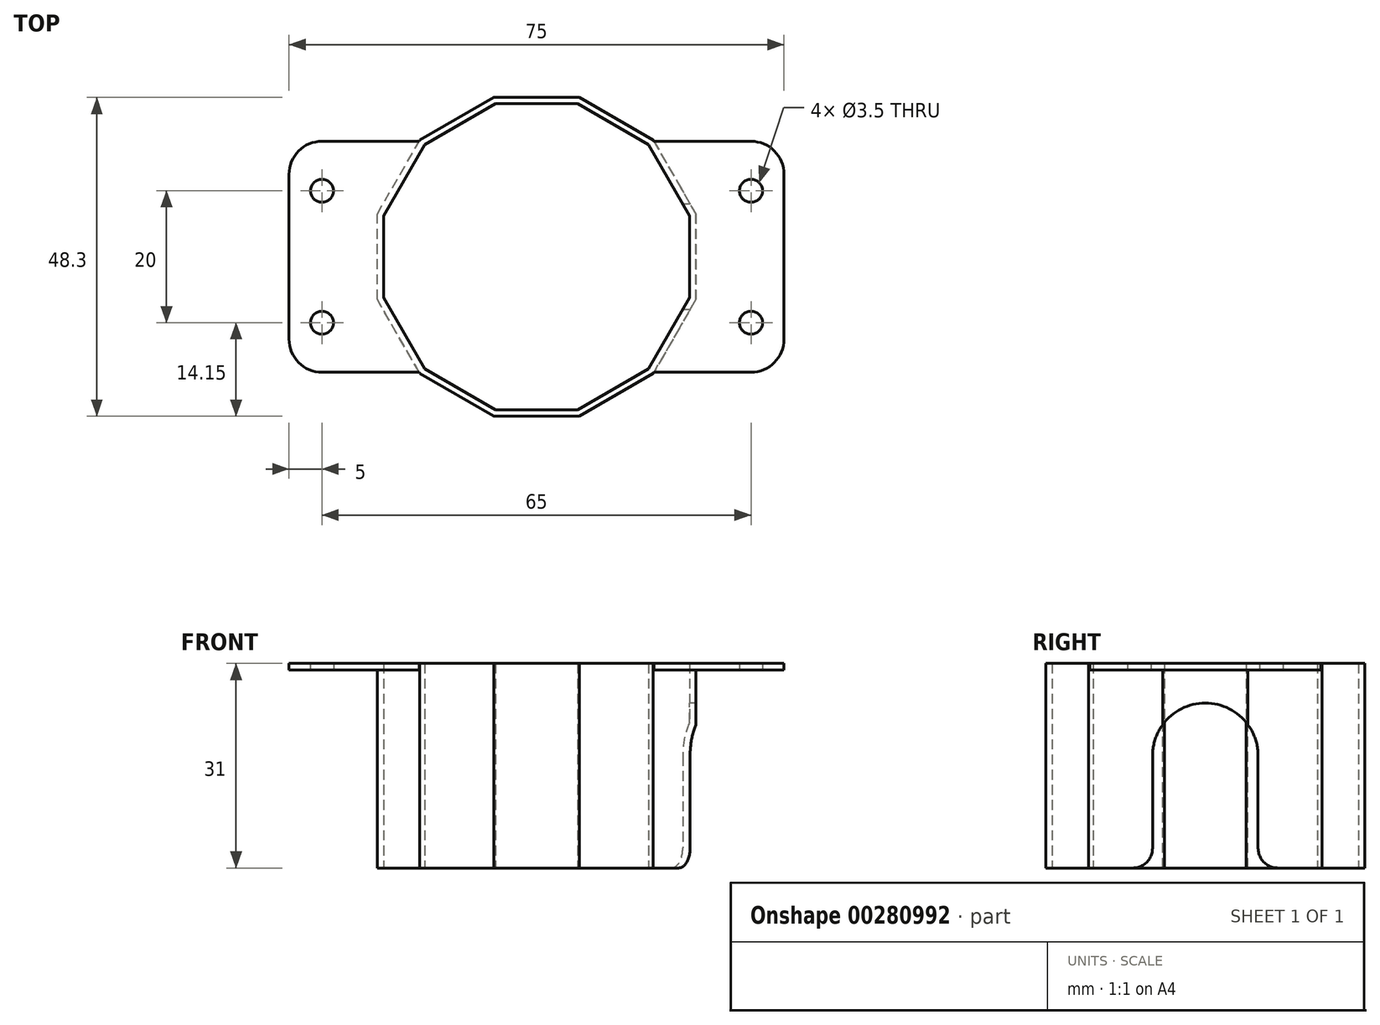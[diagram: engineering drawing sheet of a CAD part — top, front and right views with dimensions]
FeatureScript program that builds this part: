
annotation { "Feature Type Name" : "Feature", "Feature Type Description" : "" }
export const myFeature = defineFeature(function(context is Context, id is Id, definition is map)
    precondition{}
    {
        {
            var Q0;
            Q0=qCreatedBy(makeId("Top.planeOp"),FACE);
            var sketch = newSketch(context, id + "F0", { "sketchPlane" : qUnion([Q0])});
            skLineSegment(sketch, "E0.bottom", {"start": v(37.5, -17.5) * mm, "end": v(-37.5, -17.5) * mm});
            skLineSegment(sketch, "E0.top", {"start": v(37.5, 17.5) * mm, "end": v(-37.5, 17.5) * mm});
            skLineSegment(sketch, "E0.left", {"start": v(37.5, -17.5) * mm, "end": v(37.5, 17.5) * mm});
            skLineSegment(sketch, "E0.right", {"start": v(-37.5, -17.5) * mm, "end": v(-37.5, 17.5) * mm});
            skPoint(sketch, "E0.middle", {"position": v(0, 0) * mm});
            skSolve(sketch);
        }
        {
            var Q0;
            Q0 = qSketchRegion(id + "F0", true);
            extrude(context, id + "F1", {"entities" : qUnion([Q0]), "depth" : 1 * mm});
        }
        {
            var Q0;
            Q0=qCreatedBy(makeId("Top.planeOp"),FACE);
            var sketch = newSketch(context, id + "F2", { "sketchPlane" : qUnion([Q0])});
            skCircle(sketch, "E1.cCircle", {"center": v(0, 0) * mm, "radius": 25 * mm, "construction": true});
            skLineSegment(sketch, "E1.0", {"start": v(17.68, 17.68) * mm, "end": v(24.15, 6.47) * mm});
            skLineSegment(sketch, "E1.1", {"start": v(24.15, 6.47) * mm, "end": v(24.15, -6.47) * mm});
            skLineSegment(sketch, "E1.2", {"start": v(24.15, -6.47) * mm, "end": v(17.68, -17.68) * mm});
            skLineSegment(sketch, "E1.3", {"start": v(17.68, -17.68) * mm, "end": v(6.47, -24.15) * mm});
            skLineSegment(sketch, "E1.4", {"start": v(6.47, -24.15) * mm, "end": v(-6.47, -24.15) * mm});
            skLineSegment(sketch, "E1.5", {"start": v(-6.47, -24.15) * mm, "end": v(-17.68, -17.68) * mm});
            skLineSegment(sketch, "E1.6", {"start": v(-17.68, -17.68) * mm, "end": v(-24.15, -6.47) * mm});
            skLineSegment(sketch, "E1.7", {"start": v(-24.15, -6.47) * mm, "end": v(-24.15, 6.47) * mm});
            skLineSegment(sketch, "E1.8", {"start": v(-24.15, 6.47) * mm, "end": v(-17.68, 17.68) * mm});
            skLineSegment(sketch, "E1.9", {"start": v(-17.68, 17.68) * mm, "end": v(-6.47, 24.15) * mm});
            skLineSegment(sketch, "E1.10", {"start": v(-6.47, 24.15) * mm, "end": v(6.47, 24.15) * mm});
            skLineSegment(sketch, "E1.11", {"start": v(6.47, 24.15) * mm, "end": v(17.68, 17.68) * mm});
            skPoint(sketch, "E2", {"position": v(0, 24.15) * mm});
            skSolve(sketch);
        }
        {
            var Q0;
            Q0 = qSketchRegion(id + "F2", true);
            extrude(context, id + "F3", {"entities" : qUnion([Q0]), "operationType" : NewBodyOperationType.ADD, "oppositeDirection" : true, "depth" : 30 * mm});
        }
        {
            var Q0;
            Q0=makeQuery(id+"F3.opExtrude","CAP_FACE",FACE,{"disambiguationData":[OSD([sQuery(id+"F2.wireOp",EDGE,"E1.0"),sQuery(id+"F2.wireOp",EDGE,"E1.1"),sQuery(id+"F2.wireOp",EDGE,"E1.2"),sQuery(id+"F2.wireOp",EDGE,"E1.3"),sQuery(id+"F2.wireOp",EDGE,"E1.4"),sQuery(id+"F2.wireOp",EDGE,"E1.5"),sQuery(id+"F2.wireOp",EDGE,"E1.6"),sQuery(id+"F2.wireOp",EDGE,"E1.7"),sQuery(id+"F2.wireOp",EDGE,"E1.8"),sQuery(id+"F2.wireOp",EDGE,"E1.9"),sQuery(id+"F2.wireOp",EDGE,"E1.10"),sQuery(id+"F2.wireOp",EDGE,"E1.11")])],"isStart":false});
            var sketch = newSketch(context, id + "F4", { "sketchPlane" : qUnion([Q0])});
            skCircle(sketch, "E3.cCircle", {"center": v(0, 0) * mm, "radius": 24 * mm, "construction": true});
            skLineSegment(sketch, "E3.0", {"start": v(16.97, -16.97) * mm, "end": v(6.21, -23.18) * mm});
            skLineSegment(sketch, "E3.1", {"start": v(6.21, -23.18) * mm, "end": v(-6.21, -23.18) * mm});
            skLineSegment(sketch, "E3.2", {"start": v(-6.21, -23.18) * mm, "end": v(-16.97, -16.97) * mm});
            skLineSegment(sketch, "E3.3", {"start": v(-16.97, -16.97) * mm, "end": v(-23.18, -6.21) * mm});
            skLineSegment(sketch, "E3.4", {"start": v(-23.18, -6.21) * mm, "end": v(-23.18, 6.21) * mm});
            skLineSegment(sketch, "E3.5", {"start": v(-23.18, 6.21) * mm, "end": v(-16.97, 16.97) * mm});
            skLineSegment(sketch, "E3.6", {"start": v(-16.97, 16.97) * mm, "end": v(-6.21, 23.18) * mm});
            skLineSegment(sketch, "E3.7", {"start": v(-6.21, 23.18) * mm, "end": v(6.21, 23.18) * mm});
            skLineSegment(sketch, "E3.8", {"start": v(6.21, 23.18) * mm, "end": v(16.97, 16.97) * mm});
            skLineSegment(sketch, "E3.9", {"start": v(16.97, 16.97) * mm, "end": v(23.18, 6.21) * mm});
            skLineSegment(sketch, "E3.10", {"start": v(23.18, 6.21) * mm, "end": v(23.18, -6.21) * mm});
            skLineSegment(sketch, "E3.11", {"start": v(23.18, -6.21) * mm, "end": v(16.97, -16.97) * mm});
            skPoint(sketch, "E4", {"position": v(0, 23.18) * mm});
            skSolve(sketch);
        }
        {
            var Q0;
            Q0 = qSketchRegion(id + "F4", true);
            extrude(context, id + "F5", {"entities" : qUnion([Q0]), "operationType" : NewBodyOperationType.REMOVE, "oppositeDirection" : true, "depth" : 35 * mm});
        }
        {
            var Q0;
            Q0=makeQuery(id+"F1.opExtrude","SWEPT_EDGE",EDGE,{"disambiguationData":[OSD([sQuery(id+"F0.wireOp",EDGE,"E0.bottom"),sQuery(id+"F0.wireOp",EDGE,"E0.left")])]});
            var Q1;
            Q1=makeQuery(id+"F1.opExtrude","SWEPT_EDGE",EDGE,{"disambiguationData":[OSD([sQuery(id+"F0.wireOp",EDGE,"E0.top"),sQuery(id+"F0.wireOp",EDGE,"E0.left")])]});
            var Q2;
            Q2=makeQuery(id+"F1.opExtrude","SWEPT_EDGE",EDGE,{"disambiguationData":[OSD([sQuery(id+"F0.wireOp",EDGE,"E0.bottom"),sQuery(id+"F0.wireOp",EDGE,"E0.right")])]});
            var Q3;
            Q3=makeQuery(id+"F1.opExtrude","SWEPT_EDGE",EDGE,{"disambiguationData":[OSD([sQuery(id+"F0.wireOp",EDGE,"E0.top"),sQuery(id+"F0.wireOp",EDGE,"E0.right")])]});
            fillet(context, id + "F6", {"entities" : qUnion([Q0, Q1, Q2, Q3]), "radius" : 5 * mm, "tangentPropagation" : true, "allowEdgeOverflow" : false});
        }
        {
            var Q0;
            Q0=qCreatedBy(makeId("Top.planeOp"),FACE);
            var sketch = newSketch(context, id + "F7", { "sketchPlane" : qUnion([Q0])});
            skCircle(sketch, "E5", {"center": v(-32.5, 10) * mm, "radius": 1.75 * mm});
            skCircle(sketch, "E6", {"center": v(-32.5, -10) * mm, "radius": 1.75 * mm});
            skCircle(sketch, "E7", {"center": v(32.5, -10) * mm, "radius": 1.75 * mm});
            skCircle(sketch, "E8", {"center": v(32.5, 10) * mm, "radius": 1.75 * mm});
            skSolve(sketch);
        }
        {
            var Q0;
            Q0 = qSketchRegion(id + "F7", true);
            extrude(context, id + "F8", {"entities" : qUnion([Q0]), "operationType" : NewBodyOperationType.REMOVE, "depth" : 25 * mm});
        }
        {
            var Q0;
            Q0 = qSketchRegion(id + "F2", true);
            extrude(context, id + "F9", {"entities" : qUnion([Q0]), "operationType" : NewBodyOperationType.ADD, "depth" : 1 * mm});
        }
        {
            var Q0;
            Q0 = qSketchRegion(id + "F4", true);
            extrude(context, id + "F10", {"entities" : qUnion([Q0]), "operationType" : NewBodyOperationType.REMOVE, "oppositeDirection" : true, "depth" : 65.4 * mm});
        }
        {
            var Q0;
            Q0=qCreatedBy(makeId("Front.planeOp"),FACE);
            var sketch = newSketch(context, id + "F11", { "sketchPlane" : qUnion([Q0])});
            skLineSegment(sketch, "E9", {"start": v(0, 43.4) * mm, "end": v(0, -71.07) * mm, "construction": true});
            skSolve(sketch);
        }
        {
            var Q0;
            Q0=qCreatedBy(makeId("Right.planeOp"),FACE);
            var sketch = newSketch(context, id + "F12", { "sketchPlane" : qUnion([Q0])});
            skCircle(sketch, "E10", {"center": v(0, -13) * mm, "radius": 8 * mm});
            skLineSegment(sketch, "E11", {"start": v(-8, -13) * mm, "end": v(-8, -36.3) * mm});
            skLineSegment(sketch, "E12", {"start": v(8, -13) * mm, "end": v(8, -37.1) * mm});
            skLineSegment(sketch, "E13", {"start": v(8, -37.1) * mm, "end": v(-8, -36.3) * mm});
            skSolve(sketch);
        }
        {
            var Q0;
            Q0 = qSketchRegion(id + "F12", true);
            extrude(context, id + "F13", {"entities" : qUnion([Q0]), "operationType" : NewBodyOperationType.REMOVE, "depth" : 35.6 * mm});
        }
        {
            var Q0;
            {var subQ0=sQuery(id+"F12.wireOp",EDGE,"E12");var subQ3=sQuery(id+"F2.wireOp",EDGE,"E1.10");var subQ5=sQuery(id+"F2.wireOp",EDGE,"E1.0");var subQ9=makeQuery(id+"F3.opExtrude","SWEPT_FACE",FACE,{"disambiguationData":[OSD([subQ5])]});var subQ13=sQuery(id+"F2.wireOp",EDGE,"E1.11");var subQ24=sQuery(id+"F2.wireOp",EDGE,"E1.8");var subQ30=sQuery(id+"F2.wireOp",EDGE,"E1.9");var subQ35=sQuery(id+"F2.wireOp",EDGE,"E1.6");var subQ41=sQuery(id+"F2.wireOp",EDGE,"E1.7");var subQ46=sQuery(id+"F2.wireOp",EDGE,"E1.5");var subQ47=sQuery(id+"F2.wireOp",EDGE,"E1.4");Q0=makeQuery(id+"FE6U0NBdRi0kMCF_1.5.F13.boolean.opBoolean","INTERSECT",EDGE,{"derivedFrom":[makeQuery(id+"FE6U0NBdRi0kMCF_1.4.F13.boolean.opBoolean","SPLIT",FACE,{"disambiguationData":[TD([subQ9])],"derivedFrom":makeQuery(id+"FE6U0NBdRi0kMCF_1.3.F13.boolean.opBoolean","SPLIT",FACE,{"disambiguationData":[TD([subQ9])],"derivedFrom":makeQuery(id+"FE6U0NBdRi0kMCF_1.2.F13.boolean.opBoolean","SPLIT",FACE,{"disambiguationData":[TD([subQ9])],"derivedFrom":makeQuery(id+"FE6U0NBdRi0kMCF_1.1.F13.boolean.opBoolean","SPLIT",FACE,{"disambiguationData":[TD([subQ9])],"derivedFrom":makeQuery(id+"F3.opExtrude","CAP_FACE",FACE,{"disambiguationData":[OSD([subQ5,sQuery(id+"F2.wireOp",EDGE,"E1.1"),sQuery(id+"F2.wireOp",EDGE,"E1.2"),sQuery(id+"F2.wireOp",EDGE,"E1.3"),subQ47,subQ46,subQ35,subQ41,subQ24,subQ30,subQ3,subQ13])],"isStart":false})})})})}),makeQuery(id+"FE6U0NBdRi0kMCF_1.5.F13.opExtrude","SWEPT_FACE",FACE,{"disambiguationData":[OSD([subQ0])]})]});}
            var Q1;
            {var subQ0=sQuery(id+"F12.wireOp",EDGE,"E11");var subQ6=sQuery(id+"F2.wireOp",EDGE,"E1.0");var subQ7=makeQuery(id+"F3.opExtrude","SWEPT_FACE",FACE,{"disambiguationData":[OSD([subQ6])]});var subQ8=sQuery(id+"F2.wireOp",EDGE,"E1.8");var subQ16=sQuery(id+"F2.wireOp",EDGE,"E1.11");var subQ19=sQuery(id+"F2.wireOp",EDGE,"E1.10");var subQ23=sQuery(id+"F2.wireOp",EDGE,"E1.9");var subQ34=sQuery(id+"F2.wireOp",EDGE,"E1.6");var subQ40=sQuery(id+"F2.wireOp",EDGE,"E1.7");var subQ45=sQuery(id+"F2.wireOp",EDGE,"E1.5");var subQ46=sQuery(id+"F2.wireOp",EDGE,"E1.4");Q1=makeQuery(id+"FE6U0NBdRi0kMCF_1.4.F13.boolean.opBoolean","INTERSECT",EDGE,{"derivedFrom":[makeQuery(id+"FE6U0NBdRi0kMCF_1.3.F13.boolean.opBoolean","SPLIT",FACE,{"disambiguationData":[TD([subQ7])],"derivedFrom":makeQuery(id+"FE6U0NBdRi0kMCF_1.2.F13.boolean.opBoolean","SPLIT",FACE,{"disambiguationData":[TD([subQ7])],"derivedFrom":makeQuery(id+"FE6U0NBdRi0kMCF_1.1.F13.boolean.opBoolean","SPLIT",FACE,{"disambiguationData":[TD([subQ7])],"derivedFrom":makeQuery(id+"F3.opExtrude","CAP_FACE",FACE,{"disambiguationData":[OSD([subQ6,sQuery(id+"F2.wireOp",EDGE,"E1.1"),sQuery(id+"F2.wireOp",EDGE,"E1.2"),sQuery(id+"F2.wireOp",EDGE,"E1.3"),subQ46,subQ45,subQ34,subQ40,subQ8,subQ23,subQ19,subQ16])],"isStart":false})})})}),makeQuery(id+"FE6U0NBdRi0kMCF_1.4.F13.opExtrude","SWEPT_FACE",FACE,{"disambiguationData":[OSD([subQ0])]})]});}
            var Q2;
            {var subQ0=sQuery(id+"F12.wireOp",EDGE,"E12");var subQ6=sQuery(id+"F2.wireOp",EDGE,"E1.0");var subQ7=makeQuery(id+"F3.opExtrude","SWEPT_FACE",FACE,{"disambiguationData":[OSD([subQ6])]});var subQ8=sQuery(id+"F2.wireOp",EDGE,"E1.8");var subQ16=sQuery(id+"F2.wireOp",EDGE,"E1.11");var subQ19=sQuery(id+"F2.wireOp",EDGE,"E1.10");var subQ23=sQuery(id+"F2.wireOp",EDGE,"E1.9");var subQ35=sQuery(id+"F2.wireOp",EDGE,"E1.6");var subQ41=sQuery(id+"F2.wireOp",EDGE,"E1.7");var subQ46=sQuery(id+"F2.wireOp",EDGE,"E1.5");var subQ47=sQuery(id+"F2.wireOp",EDGE,"E1.4");Q2=makeQuery(id+"FE6U0NBdRi0kMCF_1.4.F13.boolean.opBoolean","INTERSECT",EDGE,{"derivedFrom":[makeQuery(id+"FE6U0NBdRi0kMCF_1.3.F13.boolean.opBoolean","SPLIT",FACE,{"disambiguationData":[TD([subQ7])],"derivedFrom":makeQuery(id+"FE6U0NBdRi0kMCF_1.2.F13.boolean.opBoolean","SPLIT",FACE,{"disambiguationData":[TD([subQ7])],"derivedFrom":makeQuery(id+"FE6U0NBdRi0kMCF_1.1.F13.boolean.opBoolean","SPLIT",FACE,{"disambiguationData":[TD([subQ7])],"derivedFrom":makeQuery(id+"F3.opExtrude","CAP_FACE",FACE,{"disambiguationData":[OSD([subQ6,sQuery(id+"F2.wireOp",EDGE,"E1.1"),sQuery(id+"F2.wireOp",EDGE,"E1.2"),sQuery(id+"F2.wireOp",EDGE,"E1.3"),subQ47,subQ46,subQ35,subQ41,subQ8,subQ23,subQ19,subQ16])],"isStart":false})})})}),makeQuery(id+"FE6U0NBdRi0kMCF_1.4.F13.opExtrude","SWEPT_FACE",FACE,{"disambiguationData":[OSD([subQ0])]})]});}
            var Q3;
            {var subQ0=sQuery(id+"F12.wireOp",EDGE,"E11");var subQ5=sQuery(id+"F2.wireOp",EDGE,"E1.9");var subQ7=sQuery(id+"F2.wireOp",EDGE,"E1.0");var subQ9=sQuery(id+"F2.wireOp",EDGE,"E1.10");var subQ11=sQuery(id+"F2.wireOp",EDGE,"E1.6");var subQ18=sQuery(id+"F2.wireOp",EDGE,"E1.8");var subQ25=makeQuery(id+"F3.opExtrude","SWEPT_FACE",FACE,{"disambiguationData":[OSD([subQ7])]});var subQ28=sQuery(id+"F2.wireOp",EDGE,"E1.7");var subQ32=sQuery(id+"F2.wireOp",EDGE,"E1.11");var subQ45=sQuery(id+"F2.wireOp",EDGE,"E1.5");var subQ46=sQuery(id+"F2.wireOp",EDGE,"E1.4");Q3=makeQuery(id+"FE6U0NBdRi0kMCF_1.3.F13.boolean.opBoolean","INTERSECT",EDGE,{"derivedFrom":[makeQuery(id+"FE6U0NBdRi0kMCF_1.2.F13.boolean.opBoolean","SPLIT",FACE,{"disambiguationData":[TD([subQ25])],"derivedFrom":makeQuery(id+"FE6U0NBdRi0kMCF_1.1.F13.boolean.opBoolean","SPLIT",FACE,{"disambiguationData":[TD([subQ25])],"derivedFrom":makeQuery(id+"F3.opExtrude","CAP_FACE",FACE,{"disambiguationData":[OSD([subQ7,sQuery(id+"F2.wireOp",EDGE,"E1.1"),sQuery(id+"F2.wireOp",EDGE,"E1.2"),sQuery(id+"F2.wireOp",EDGE,"E1.3"),subQ46,subQ45,subQ11,subQ28,subQ18,subQ5,subQ9,subQ32])],"isStart":false})})}),makeQuery(id+"FE6U0NBdRi0kMCF_1.3.F13.opExtrude","SWEPT_FACE",FACE,{"disambiguationData":[OSD([subQ0])]})]});}
            var Q4;
            {var subQ0=sQuery(id+"F12.wireOp",EDGE,"E12");var subQ5=sQuery(id+"F2.wireOp",EDGE,"E1.9");var subQ7=sQuery(id+"F2.wireOp",EDGE,"E1.0");var subQ9=sQuery(id+"F2.wireOp",EDGE,"E1.10");var subQ11=sQuery(id+"F2.wireOp",EDGE,"E1.6");var subQ18=sQuery(id+"F2.wireOp",EDGE,"E1.8");var subQ25=makeQuery(id+"F3.opExtrude","SWEPT_FACE",FACE,{"disambiguationData":[OSD([subQ7])]});var subQ28=sQuery(id+"F2.wireOp",EDGE,"E1.7");var subQ32=sQuery(id+"F2.wireOp",EDGE,"E1.11");var subQ46=sQuery(id+"F2.wireOp",EDGE,"E1.5");var subQ47=sQuery(id+"F2.wireOp",EDGE,"E1.4");Q4=makeQuery(id+"FE6U0NBdRi0kMCF_1.3.F13.boolean.opBoolean","INTERSECT",EDGE,{"derivedFrom":[makeQuery(id+"FE6U0NBdRi0kMCF_1.2.F13.boolean.opBoolean","SPLIT",FACE,{"disambiguationData":[TD([subQ25])],"derivedFrom":makeQuery(id+"FE6U0NBdRi0kMCF_1.1.F13.boolean.opBoolean","SPLIT",FACE,{"disambiguationData":[TD([subQ25])],"derivedFrom":makeQuery(id+"F3.opExtrude","CAP_FACE",FACE,{"disambiguationData":[OSD([subQ7,sQuery(id+"F2.wireOp",EDGE,"E1.1"),sQuery(id+"F2.wireOp",EDGE,"E1.2"),sQuery(id+"F2.wireOp",EDGE,"E1.3"),subQ47,subQ46,subQ11,subQ28,subQ18,subQ5,subQ9,subQ32])],"isStart":false})})}),makeQuery(id+"FE6U0NBdRi0kMCF_1.3.F13.opExtrude","SWEPT_FACE",FACE,{"disambiguationData":[OSD([subQ0])]})]});}
            var Q5;
            {var subQ0=sQuery(id+"F12.wireOp",EDGE,"E11");var subQ1=sQuery(id+"F2.wireOp",EDGE,"E1.0");var subQ2=sQuery(id+"F2.wireOp",EDGE,"E1.10");var subQ6=sQuery(id+"F2.wireOp",EDGE,"E1.5");var subQ8=sQuery(id+"F2.wireOp",EDGE,"E1.6");var subQ12=sQuery(id+"F2.wireOp",EDGE,"E1.4");var subQ14=sQuery(id+"F2.wireOp",EDGE,"E1.8");var subQ16=sQuery(id+"F2.wireOp",EDGE,"E1.9");var subQ17=sQuery(id+"F2.wireOp",EDGE,"E1.11");var subQ18=sQuery(id+"F2.wireOp",EDGE,"E1.7");Q5=makeQuery(id+"FE6U0NBdRi0kMCF_1.2.F13.boolean.opBoolean","INTERSECT",EDGE,{"derivedFrom":[makeQuery(id+"FE6U0NBdRi0kMCF_1.1.F13.boolean.opBoolean","SPLIT",FACE,{"disambiguationData":[TD([makeQuery(id+"F3.opExtrude","SWEPT_FACE",FACE,{"disambiguationData":[OSD([subQ1])]})])],"derivedFrom":makeQuery(id+"F3.opExtrude","CAP_FACE",FACE,{"disambiguationData":[OSD([subQ1,sQuery(id+"F2.wireOp",EDGE,"E1.1"),sQuery(id+"F2.wireOp",EDGE,"E1.2"),sQuery(id+"F2.wireOp",EDGE,"E1.3"),subQ12,subQ6,subQ8,subQ18,subQ14,subQ16,subQ2,subQ17])],"isStart":false})}),makeQuery(id+"FE6U0NBdRi0kMCF_1.2.F13.opExtrude","SWEPT_FACE",FACE,{"disambiguationData":[OSD([subQ0])]})]});}
            var Q6;
            Q6=makeQuery(id+"FE6U0NBdRi0kMCF_1.1.F13.boolean.opBoolean","INTERSECT",EDGE,{"derivedFrom":[makeQuery(id+"F3.opExtrude","CAP_FACE",FACE,{"disambiguationData":[OSD([sQuery(id+"F2.wireOp",EDGE,"E1.0"),sQuery(id+"F2.wireOp",EDGE,"E1.1"),sQuery(id+"F2.wireOp",EDGE,"E1.2"),sQuery(id+"F2.wireOp",EDGE,"E1.3"),sQuery(id+"F2.wireOp",EDGE,"E1.4"),sQuery(id+"F2.wireOp",EDGE,"E1.5"),sQuery(id+"F2.wireOp",EDGE,"E1.6"),sQuery(id+"F2.wireOp",EDGE,"E1.7"),sQuery(id+"F2.wireOp",EDGE,"E1.8"),sQuery(id+"F2.wireOp",EDGE,"E1.9"),sQuery(id+"F2.wireOp",EDGE,"E1.10"),sQuery(id+"F2.wireOp",EDGE,"E1.11")])],"isStart":false}),makeQuery(id+"FE6U0NBdRi0kMCF_1.1.F13.opExtrude","SWEPT_FACE",FACE,{"disambiguationData":[OSD([sQuery(id+"F12.wireOp",EDGE,"E11")])]})]});
            var Q7;
            {var subQ0=sQuery(id+"F12.wireOp",EDGE,"E12");var subQ1=sQuery(id+"F2.wireOp",EDGE,"E1.0");var subQ2=sQuery(id+"F2.wireOp",EDGE,"E1.10");var subQ6=sQuery(id+"F2.wireOp",EDGE,"E1.5");var subQ8=sQuery(id+"F2.wireOp",EDGE,"E1.6");var subQ12=sQuery(id+"F2.wireOp",EDGE,"E1.4");var subQ14=sQuery(id+"F2.wireOp",EDGE,"E1.8");var subQ16=sQuery(id+"F2.wireOp",EDGE,"E1.9");var subQ17=sQuery(id+"F2.wireOp",EDGE,"E1.11");var subQ18=sQuery(id+"F2.wireOp",EDGE,"E1.7");Q7=makeQuery(id+"FE6U0NBdRi0kMCF_1.2.F13.boolean.opBoolean","INTERSECT",EDGE,{"derivedFrom":[makeQuery(id+"FE6U0NBdRi0kMCF_1.1.F13.boolean.opBoolean","SPLIT",FACE,{"disambiguationData":[TD([makeQuery(id+"F3.opExtrude","SWEPT_FACE",FACE,{"disambiguationData":[OSD([subQ1])]})])],"derivedFrom":makeQuery(id+"F3.opExtrude","CAP_FACE",FACE,{"disambiguationData":[OSD([subQ1,sQuery(id+"F2.wireOp",EDGE,"E1.1"),sQuery(id+"F2.wireOp",EDGE,"E1.2"),sQuery(id+"F2.wireOp",EDGE,"E1.3"),subQ12,subQ6,subQ8,subQ18,subQ14,subQ16,subQ2,subQ17])],"isStart":false})}),makeQuery(id+"FE6U0NBdRi0kMCF_1.2.F13.opExtrude","SWEPT_FACE",FACE,{"disambiguationData":[OSD([subQ0])]})]});}
            var Q8;
            Q8=makeQuery(id+"FE6U0NBdRi0kMCF_1.1.F13.boolean.opBoolean","INTERSECT",EDGE,{"derivedFrom":[makeQuery(id+"F3.opExtrude","CAP_FACE",FACE,{"disambiguationData":[OSD([sQuery(id+"F2.wireOp",EDGE,"E1.0"),sQuery(id+"F2.wireOp",EDGE,"E1.1"),sQuery(id+"F2.wireOp",EDGE,"E1.2"),sQuery(id+"F2.wireOp",EDGE,"E1.3"),sQuery(id+"F2.wireOp",EDGE,"E1.4"),sQuery(id+"F2.wireOp",EDGE,"E1.5"),sQuery(id+"F2.wireOp",EDGE,"E1.6"),sQuery(id+"F2.wireOp",EDGE,"E1.7"),sQuery(id+"F2.wireOp",EDGE,"E1.8"),sQuery(id+"F2.wireOp",EDGE,"E1.9"),sQuery(id+"F2.wireOp",EDGE,"E1.10"),sQuery(id+"F2.wireOp",EDGE,"E1.11")])],"isStart":false}),makeQuery(id+"FE6U0NBdRi0kMCF_1.1.F13.opExtrude","SWEPT_FACE",FACE,{"disambiguationData":[OSD([sQuery(id+"F12.wireOp",EDGE,"E12")])]})]});
            var Q9;
            Q9=makeQuery(id+"F13.boolean.opBoolean","INTERSECT",EDGE,{"derivedFrom":[makeQuery(id+"F3.opExtrude","CAP_FACE",FACE,{"disambiguationData":[OSD([sQuery(id+"F2.wireOp",EDGE,"E1.0"),sQuery(id+"F2.wireOp",EDGE,"E1.1"),sQuery(id+"F2.wireOp",EDGE,"E1.2"),sQuery(id+"F2.wireOp",EDGE,"E1.3"),sQuery(id+"F2.wireOp",EDGE,"E1.4"),sQuery(id+"F2.wireOp",EDGE,"E1.5"),sQuery(id+"F2.wireOp",EDGE,"E1.6"),sQuery(id+"F2.wireOp",EDGE,"E1.7"),sQuery(id+"F2.wireOp",EDGE,"E1.8"),sQuery(id+"F2.wireOp",EDGE,"E1.9"),sQuery(id+"F2.wireOp",EDGE,"E1.10"),sQuery(id+"F2.wireOp",EDGE,"E1.11")])],"isStart":false}),makeQuery(id+"F13.opExtrude","SWEPT_FACE",FACE,{"disambiguationData":[OSD([sQuery(id+"F12.wireOp",EDGE,"E11")])]})]});
            var Q10;
            Q10=makeQuery(id+"F13.boolean.opBoolean","INTERSECT",EDGE,{"derivedFrom":[makeQuery(id+"F3.opExtrude","CAP_FACE",FACE,{"disambiguationData":[OSD([sQuery(id+"F2.wireOp",EDGE,"E1.0"),sQuery(id+"F2.wireOp",EDGE,"E1.1"),sQuery(id+"F2.wireOp",EDGE,"E1.2"),sQuery(id+"F2.wireOp",EDGE,"E1.3"),sQuery(id+"F2.wireOp",EDGE,"E1.4"),sQuery(id+"F2.wireOp",EDGE,"E1.5"),sQuery(id+"F2.wireOp",EDGE,"E1.6"),sQuery(id+"F2.wireOp",EDGE,"E1.7"),sQuery(id+"F2.wireOp",EDGE,"E1.8"),sQuery(id+"F2.wireOp",EDGE,"E1.9"),sQuery(id+"F2.wireOp",EDGE,"E1.10"),sQuery(id+"F2.wireOp",EDGE,"E1.11")])],"isStart":false}),makeQuery(id+"F13.opExtrude","SWEPT_FACE",FACE,{"disambiguationData":[OSD([sQuery(id+"F12.wireOp",EDGE,"E12")])]})]});
            var Q11;
            {var subQ0=sQuery(id+"F12.wireOp",EDGE,"E11");var subQ3=sQuery(id+"F2.wireOp",EDGE,"E1.10");var subQ5=sQuery(id+"F2.wireOp",EDGE,"E1.0");var subQ9=makeQuery(id+"F3.opExtrude","SWEPT_FACE",FACE,{"disambiguationData":[OSD([subQ5])]});var subQ13=sQuery(id+"F2.wireOp",EDGE,"E1.11");var subQ23=sQuery(id+"F2.wireOp",EDGE,"E1.8");var subQ29=sQuery(id+"F2.wireOp",EDGE,"E1.9");var subQ34=sQuery(id+"F2.wireOp",EDGE,"E1.6");var subQ40=sQuery(id+"F2.wireOp",EDGE,"E1.7");var subQ45=sQuery(id+"F2.wireOp",EDGE,"E1.5");var subQ46=sQuery(id+"F2.wireOp",EDGE,"E1.4");Q11=makeQuery(id+"FE6U0NBdRi0kMCF_1.5.F13.boolean.opBoolean","INTERSECT",EDGE,{"derivedFrom":[makeQuery(id+"FE6U0NBdRi0kMCF_1.4.F13.boolean.opBoolean","SPLIT",FACE,{"disambiguationData":[TD([subQ9])],"derivedFrom":makeQuery(id+"FE6U0NBdRi0kMCF_1.3.F13.boolean.opBoolean","SPLIT",FACE,{"disambiguationData":[TD([subQ9])],"derivedFrom":makeQuery(id+"FE6U0NBdRi0kMCF_1.2.F13.boolean.opBoolean","SPLIT",FACE,{"disambiguationData":[TD([subQ9])],"derivedFrom":makeQuery(id+"FE6U0NBdRi0kMCF_1.1.F13.boolean.opBoolean","SPLIT",FACE,{"disambiguationData":[TD([subQ9])],"derivedFrom":makeQuery(id+"F3.opExtrude","CAP_FACE",FACE,{"disambiguationData":[OSD([subQ5,sQuery(id+"F2.wireOp",EDGE,"E1.1"),sQuery(id+"F2.wireOp",EDGE,"E1.2"),sQuery(id+"F2.wireOp",EDGE,"E1.3"),subQ46,subQ45,subQ34,subQ40,subQ23,subQ29,subQ3,subQ13])],"isStart":false})})})})}),makeQuery(id+"FE6U0NBdRi0kMCF_1.5.F13.opExtrude","SWEPT_FACE",FACE,{"disambiguationData":[OSD([subQ0])]})]});}
            fillet(context, id + "F14", {"entities" : qUnion([Q0, Q1, Q2, Q3, Q4, Q5, Q6, Q7, Q8, Q9, Q10, Q11]), "radius" : 3 * mm, "tangentPropagation" : true, "allowEdgeOverflow" : false});
        }
    });
